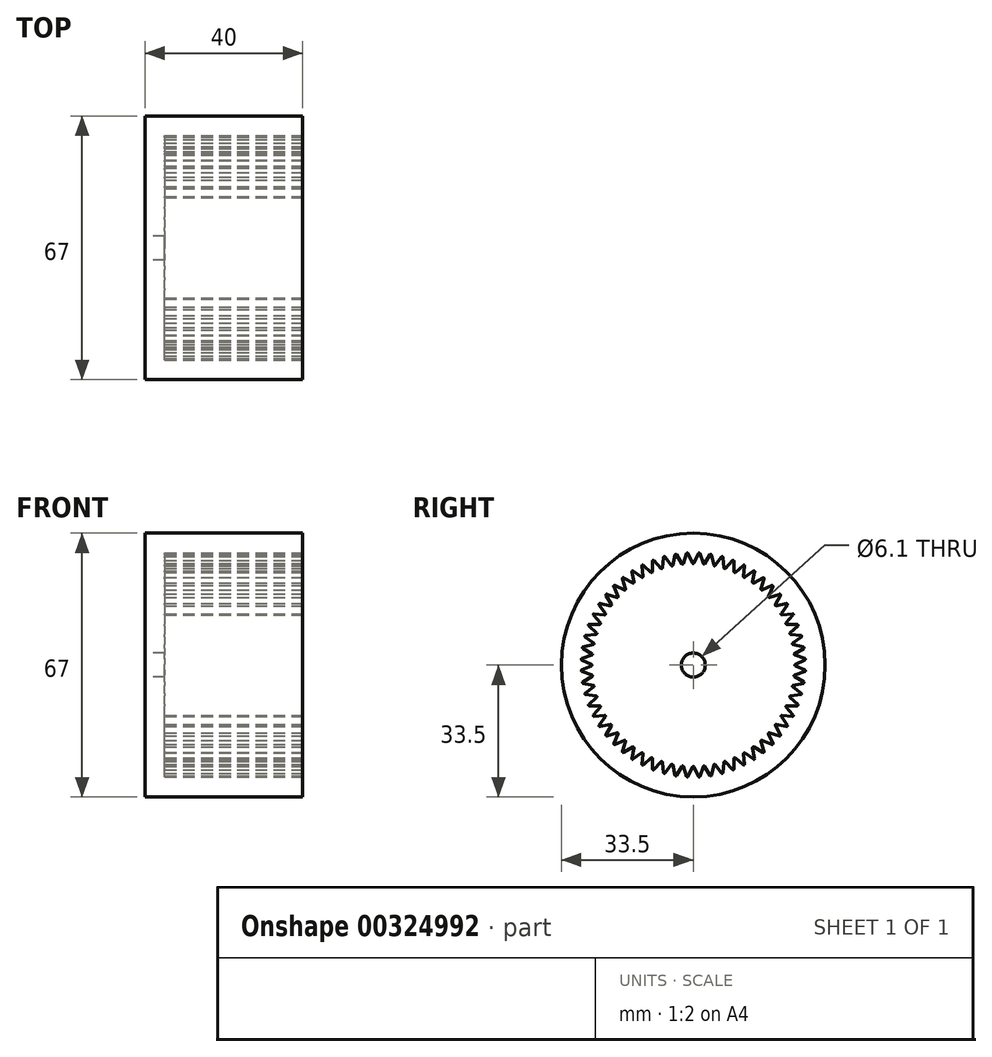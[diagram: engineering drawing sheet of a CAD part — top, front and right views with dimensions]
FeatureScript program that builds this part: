
annotation { "Feature Type Name" : "Feature", "Feature Type Description" : "" }
export const myFeature = defineFeature(function(context is Context, id is Id, definition is map)
    precondition{}
    {
        {
            var Q0;
            Q0=qCreatedBy(makeId("Right.planeOp"),FACE);
            var sketch = newSketch(context, id + "F0", { "sketchPlane" : qUnion([Q0])});
            skCircle(sketch, "E0", {"center": v(0, 0) * mm, "radius": 33.5 * mm});
            skSolve(sketch);
        }
        {
            var Q0;
            Q0 = qSketchRegion(id + "F0", true);
            extrude(context, id + "F1", {"entities" : qUnion([Q0]), "depth" : 40 * mm});
        }
        {
            var Q0;
            Q0=makeQuery(id+"F1.opExtrude","CAP_FACE",FACE,{"disambiguationData":[OSD([sQuery(id+"F0.wireOp",EDGE,"E0")])],"isStart":false});
            var sketch = newSketch(context, id + "F2", { "sketchPlane" : qUnion([Q0])});
            skLineSegment(sketch, "E1", {"start": v(-1.3, 28.34) * mm, "end": v(-0.18, 25.9) * mm});
            skLineSegment(sketch, "E2.MirrorCS", {"start": v(1.3, 28.34) * mm, "end": v(0.18, 25.9) * mm});
            skCircle(sketch, "E3", {"center": v(0, 0) * mm, "radius": 28.5 * mm, "construction": true});
            skPoint(sketch, "E4.visualSharp", {"position": v(0, 25.5) * mm});
            skArc(sketch, "E4.filletArc", {"start": v(-0.18, 25.9) * mm, "mid": v(0, 25.78) * mm, "end": v(0.18, 25.9) * mm});
            skArc(sketch, "E5", {"start": v(-1.3, 28.34) * mm, "mid": v(-1.5, 28.46) * mm, "end": v(-1.67, 28.32) * mm});
            skPoint(sketch, "E6.1.0", {"position": v(-2.67, 25.36) * mm});
            skLineSegment(sketch, "E6.1.1", {"start": v(-1.67, 28.32) * mm, "end": v(-2.53, 25.78) * mm});
            skLineSegment(sketch, "E6.1.2", {"start": v(-4.25, 28.05) * mm, "end": v(-2.89, 25.74) * mm});
            skArc(sketch, "E6.1.3", {"start": v(-2.89, 25.74) * mm, "mid": v(-2.7, 25.64) * mm, "end": v(-2.53, 25.78) * mm});
            skArc(sketch, "E6.1.4", {"start": v(-4.25, 28.05) * mm, "mid": v(-4.46, 28.15) * mm, "end": v(-4.62, 28) * mm});
            skPoint(sketch, "E6.2.0", {"position": v(-5.3, 24.94) * mm});
            skLineSegment(sketch, "E6.2.1", {"start": v(-4.62, 28) * mm, "end": v(-5.2, 25.37) * mm});
            skLineSegment(sketch, "E6.2.2", {"start": v(-7.16, 27.45) * mm, "end": v(-5.56, 25.3) * mm});
            skArc(sketch, "E6.2.3", {"start": v(-5.56, 25.3) * mm, "mid": v(-5.36, 25.22) * mm, "end": v(-5.2, 25.37) * mm});
            skArc(sketch, "E6.2.4", {"start": v(-7.16, 27.45) * mm, "mid": v(-7.38, 27.53) * mm, "end": v(-7.52, 27.36) * mm});
            skPoint(sketch, "E6.3.0", {"position": v(-7.88, 24.25) * mm});
            skLineSegment(sketch, "E6.3.1", {"start": v(-7.52, 27.36) * mm, "end": v(-7.83, 24.69) * mm});
            skLineSegment(sketch, "E6.3.2", {"start": v(-10, 26.56) * mm, "end": v(-8.18, 24.57) * mm});
            skArc(sketch, "E6.3.3", {"start": v(-8.18, 24.57) * mm, "mid": v(-7.97, 24.52) * mm, "end": v(-7.83, 24.69) * mm});
            skArc(sketch, "E6.3.4", {"start": v(-10, 26.56) * mm, "mid": v(-10.21, 26.6) * mm, "end": v(-10.34, 26.42) * mm});
            skPoint(sketch, "E6.4.0", {"position": v(-10.37, 23.3) * mm});
            skLineSegment(sketch, "E6.4.1", {"start": v(-10.34, 26.42) * mm, "end": v(-10.37, 23.73) * mm});
            skLineSegment(sketch, "E6.4.2", {"start": v(-12.72, 25.37) * mm, "end": v(-10.7, 23.59) * mm});
            skArc(sketch, "E6.4.3", {"start": v(-10.7, 23.59) * mm, "mid": v(-10.49, 23.55) * mm, "end": v(-10.37, 23.73) * mm});
            skArc(sketch, "E6.4.4", {"start": v(-12.72, 25.37) * mm, "mid": v(-12.94, 25.4) * mm, "end": v(-13.05, 25.2) * mm});
            skPoint(sketch, "E6.5.0", {"position": v(-12.75, 22.08) * mm});
            skLineSegment(sketch, "E6.5.1", {"start": v(-13.05, 25.2) * mm, "end": v(-12.8, 22.52) * mm});
            skLineSegment(sketch, "E6.5.2", {"start": v(-15.3, 23.9) * mm, "end": v(-13.1, 22.34) * mm});
            skArc(sketch, "E6.5.3", {"start": v(-13.1, 22.34) * mm, "mid": v(-12.9, 22.33) * mm, "end": v(-12.8, 22.52) * mm});
            skArc(sketch, "E6.5.4", {"start": v(-15.3, 23.9) * mm, "mid": v(-15.52, 23.9) * mm, "end": v(-15.6, 23.7) * mm});
            skPoint(sketch, "E6.6.0", {"position": v(-14.99, 20.63) * mm});
            skLineSegment(sketch, "E6.6.1", {"start": v(-15.6, 23.7) * mm, "end": v(-15.08, 21.06) * mm});
            skLineSegment(sketch, "E6.6.2", {"start": v(-17.71, 22.17) * mm, "end": v(-15.37, 20.85) * mm});
            skArc(sketch, "E6.6.3", {"start": v(-15.37, 20.85) * mm, "mid": v(-15.15, 20.86) * mm, "end": v(-15.08, 21.06) * mm});
            skArc(sketch, "E6.6.4", {"start": v(-17.71, 22.17) * mm, "mid": v(-17.94, 22.15) * mm, "end": v(-18, 21.93) * mm});
            skPoint(sketch, "E6.7.0", {"position": v(-17.06, 18.95) * mm});
            skLineSegment(sketch, "E6.7.1", {"start": v(-18, 21.93) * mm, "end": v(-17.2, 19.37) * mm});
            skLineSegment(sketch, "E6.7.2", {"start": v(-19.93, 20.2) * mm, "end": v(-17.46, 19.12) * mm});
            skArc(sketch, "E6.7.3", {"start": v(-17.46, 19.12) * mm, "mid": v(-17.25, 19.16) * mm, "end": v(-17.2, 19.37) * mm});
            skArc(sketch, "E6.7.4", {"start": v(-19.93, 20.2) * mm, "mid": v(-20.15, 20.15) * mm, "end": v(-20.2, 19.93) * mm});
            skPoint(sketch, "E6.8.0", {"position": v(-18.95, 17.06) * mm});
            skLineSegment(sketch, "E6.8.1", {"start": v(-20.2, 19.93) * mm, "end": v(-19.12, 17.46) * mm});
            skLineSegment(sketch, "E6.8.2", {"start": v(-21.93, 18) * mm, "end": v(-19.37, 17.2) * mm});
            skArc(sketch, "E6.8.3", {"start": v(-19.37, 17.2) * mm, "mid": v(-19.16, 17.25) * mm, "end": v(-19.12, 17.46) * mm});
            skArc(sketch, "E6.8.4", {"start": v(-21.93, 18) * mm, "mid": v(-22.15, 17.94) * mm, "end": v(-22.17, 17.71) * mm});
            skPoint(sketch, "E6.9.0", {"position": v(-20.63, 14.99) * mm});
            skLineSegment(sketch, "E6.9.1", {"start": v(-22.17, 17.71) * mm, "end": v(-20.85, 15.37) * mm});
            skLineSegment(sketch, "E6.9.2", {"start": v(-23.7, 15.6) * mm, "end": v(-21.06, 15.08) * mm});
            skArc(sketch, "E6.9.3", {"start": v(-21.06, 15.08) * mm, "mid": v(-20.86, 15.15) * mm, "end": v(-20.85, 15.37) * mm});
            skArc(sketch, "E6.9.4", {"start": v(-23.7, 15.6) * mm, "mid": v(-23.9, 15.52) * mm, "end": v(-23.9, 15.3) * mm});
            skPoint(sketch, "E6.10.0", {"position": v(-22.08, 12.75) * mm});
            skLineSegment(sketch, "E6.10.1", {"start": v(-23.9, 15.3) * mm, "end": v(-22.34, 13.1) * mm});
            skLineSegment(sketch, "E6.10.2", {"start": v(-25.2, 13.05) * mm, "end": v(-22.52, 12.8) * mm});
            skArc(sketch, "E6.10.3", {"start": v(-22.52, 12.8) * mm, "mid": v(-22.33, 12.9) * mm, "end": v(-22.34, 13.1) * mm});
            skArc(sketch, "E6.10.4", {"start": v(-25.2, 13.05) * mm, "mid": v(-25.4, 12.94) * mm, "end": v(-25.37, 12.72) * mm});
            skPoint(sketch, "E6.11.0", {"position": v(-23.3, 10.37) * mm});
            skLineSegment(sketch, "E6.11.1", {"start": v(-25.37, 12.72) * mm, "end": v(-23.59, 10.7) * mm});
            skLineSegment(sketch, "E6.11.2", {"start": v(-26.42, 10.34) * mm, "end": v(-23.73, 10.37) * mm});
            skArc(sketch, "E6.11.3", {"start": v(-23.73, 10.37) * mm, "mid": v(-23.55, 10.49) * mm, "end": v(-23.59, 10.7) * mm});
            skArc(sketch, "E6.11.4", {"start": v(-26.42, 10.34) * mm, "mid": v(-26.6, 10.21) * mm, "end": v(-26.56, 10) * mm});
            skPoint(sketch, "E6.12.0", {"position": v(-24.25, 7.88) * mm});
            skLineSegment(sketch, "E6.12.1", {"start": v(-26.56, 10) * mm, "end": v(-24.57, 8.18) * mm});
            skLineSegment(sketch, "E6.12.2", {"start": v(-27.36, 7.52) * mm, "end": v(-24.69, 7.83) * mm});
            skArc(sketch, "E6.12.3", {"start": v(-24.69, 7.83) * mm, "mid": v(-24.52, 7.97) * mm, "end": v(-24.57, 8.18) * mm});
            skArc(sketch, "E6.12.4", {"start": v(-27.36, 7.52) * mm, "mid": v(-27.53, 7.38) * mm, "end": v(-27.45, 7.16) * mm});
            skPoint(sketch, "E6.13.0", {"position": v(-24.94, 5.3) * mm});
            skLineSegment(sketch, "E6.13.1", {"start": v(-27.45, 7.16) * mm, "end": v(-25.3, 5.56) * mm});
            skLineSegment(sketch, "E6.13.2", {"start": v(-28, 4.62) * mm, "end": v(-25.37, 5.2) * mm});
            skArc(sketch, "E6.13.3", {"start": v(-25.37, 5.2) * mm, "mid": v(-25.22, 5.36) * mm, "end": v(-25.3, 5.56) * mm});
            skArc(sketch, "E6.13.4", {"start": v(-28, 4.62) * mm, "mid": v(-28.15, 4.46) * mm, "end": v(-28.05, 4.25) * mm});
            skPoint(sketch, "E6.14.0", {"position": v(-25.36, 2.67) * mm});
            skLineSegment(sketch, "E6.14.1", {"start": v(-28.05, 4.25) * mm, "end": v(-25.74, 2.89) * mm});
            skLineSegment(sketch, "E6.14.2", {"start": v(-28.32, 1.67) * mm, "end": v(-25.78, 2.53) * mm});
            skArc(sketch, "E6.14.3", {"start": v(-25.78, 2.53) * mm, "mid": v(-25.64, 2.7) * mm, "end": v(-25.74, 2.89) * mm});
            skArc(sketch, "E6.14.4", {"start": v(-28.32, 1.67) * mm, "mid": v(-28.46, 1.5) * mm, "end": v(-28.34, 1.3) * mm});
            skPoint(sketch, "E6.15.0", {"position": v(-25.5, 0) * mm});
            skLineSegment(sketch, "E6.15.1", {"start": v(-28.34, 1.3) * mm, "end": v(-25.9, 0.18) * mm});
            skLineSegment(sketch, "E6.15.2", {"start": v(-28.34, -1.3) * mm, "end": v(-25.9, -0.18) * mm});
            skArc(sketch, "E6.15.3", {"start": v(-25.9, -0.18) * mm, "mid": v(-25.78, 0) * mm, "end": v(-25.9, 0.18) * mm});
            skArc(sketch, "E6.15.4", {"start": v(-28.34, -1.3) * mm, "mid": v(-28.46, -1.5) * mm, "end": v(-28.32, -1.67) * mm});
            skPoint(sketch, "E6.16.0", {"position": v(-25.36, -2.67) * mm});
            skLineSegment(sketch, "E6.16.1", {"start": v(-28.32, -1.67) * mm, "end": v(-25.78, -2.53) * mm});
            skLineSegment(sketch, "E6.16.2", {"start": v(-28.05, -4.25) * mm, "end": v(-25.74, -2.89) * mm});
            skArc(sketch, "E6.16.3", {"start": v(-25.74, -2.89) * mm, "mid": v(-25.64, -2.7) * mm, "end": v(-25.78, -2.53) * mm});
            skArc(sketch, "E6.16.4", {"start": v(-28.05, -4.25) * mm, "mid": v(-28.15, -4.46) * mm, "end": v(-28, -4.62) * mm});
            skPoint(sketch, "E6.17.0", {"position": v(-24.94, -5.3) * mm});
            skLineSegment(sketch, "E6.17.1", {"start": v(-28, -4.62) * mm, "end": v(-25.37, -5.2) * mm});
            skLineSegment(sketch, "E6.17.2", {"start": v(-27.45, -7.16) * mm, "end": v(-25.3, -5.56) * mm});
            skArc(sketch, "E6.17.3", {"start": v(-25.3, -5.56) * mm, "mid": v(-25.22, -5.36) * mm, "end": v(-25.37, -5.2) * mm});
            skArc(sketch, "E6.17.4", {"start": v(-27.45, -7.16) * mm, "mid": v(-27.53, -7.38) * mm, "end": v(-27.36, -7.52) * mm});
            skPoint(sketch, "E6.18.0", {"position": v(-24.25, -7.88) * mm});
            skLineSegment(sketch, "E6.18.1", {"start": v(-27.36, -7.52) * mm, "end": v(-24.69, -7.83) * mm});
            skLineSegment(sketch, "E6.18.2", {"start": v(-26.56, -10) * mm, "end": v(-24.57, -8.18) * mm});
            skArc(sketch, "E6.18.3", {"start": v(-24.57, -8.18) * mm, "mid": v(-24.52, -7.97) * mm, "end": v(-24.69, -7.83) * mm});
            skArc(sketch, "E6.18.4", {"start": v(-26.56, -10) * mm, "mid": v(-26.6, -10.21) * mm, "end": v(-26.42, -10.34) * mm});
            skPoint(sketch, "E6.19.0", {"position": v(-23.3, -10.37) * mm});
            skLineSegment(sketch, "E6.19.1", {"start": v(-26.42, -10.34) * mm, "end": v(-23.73, -10.37) * mm});
            skLineSegment(sketch, "E6.19.2", {"start": v(-25.37, -12.72) * mm, "end": v(-23.59, -10.7) * mm});
            skArc(sketch, "E6.19.3", {"start": v(-23.59, -10.7) * mm, "mid": v(-23.55, -10.49) * mm, "end": v(-23.73, -10.37) * mm});
            skArc(sketch, "E6.19.4", {"start": v(-25.37, -12.72) * mm, "mid": v(-25.4, -12.94) * mm, "end": v(-25.2, -13.05) * mm});
            skPoint(sketch, "E6.20.0", {"position": v(-22.08, -12.75) * mm});
            skLineSegment(sketch, "E6.20.1", {"start": v(-25.2, -13.05) * mm, "end": v(-22.52, -12.8) * mm});
            skLineSegment(sketch, "E6.20.2", {"start": v(-23.9, -15.3) * mm, "end": v(-22.34, -13.1) * mm});
            skArc(sketch, "E6.20.3", {"start": v(-22.34, -13.1) * mm, "mid": v(-22.33, -12.9) * mm, "end": v(-22.52, -12.8) * mm});
            skArc(sketch, "E6.20.4", {"start": v(-23.9, -15.3) * mm, "mid": v(-23.9, -15.52) * mm, "end": v(-23.7, -15.6) * mm});
            skPoint(sketch, "E6.21.0", {"position": v(-20.63, -14.99) * mm});
            skLineSegment(sketch, "E6.21.1", {"start": v(-23.7, -15.6) * mm, "end": v(-21.06, -15.08) * mm});
            skLineSegment(sketch, "E6.21.2", {"start": v(-22.17, -17.71) * mm, "end": v(-20.85, -15.37) * mm});
            skArc(sketch, "E6.21.3", {"start": v(-20.85, -15.37) * mm, "mid": v(-20.86, -15.15) * mm, "end": v(-21.06, -15.08) * mm});
            skArc(sketch, "E6.21.4", {"start": v(-22.17, -17.71) * mm, "mid": v(-22.15, -17.94) * mm, "end": v(-21.93, -18) * mm});
            skPoint(sketch, "E6.22.0", {"position": v(-18.95, -17.06) * mm});
            skLineSegment(sketch, "E6.22.1", {"start": v(-21.93, -18) * mm, "end": v(-19.37, -17.2) * mm});
            skLineSegment(sketch, "E6.22.2", {"start": v(-20.2, -19.93) * mm, "end": v(-19.12, -17.46) * mm});
            skArc(sketch, "E6.22.3", {"start": v(-19.12, -17.46) * mm, "mid": v(-19.16, -17.25) * mm, "end": v(-19.37, -17.2) * mm});
            skArc(sketch, "E6.22.4", {"start": v(-20.2, -19.93) * mm, "mid": v(-20.15, -20.15) * mm, "end": v(-19.93, -20.2) * mm});
            skPoint(sketch, "E6.23.0", {"position": v(-17.06, -18.95) * mm});
            skLineSegment(sketch, "E6.23.1", {"start": v(-19.93, -20.2) * mm, "end": v(-17.46, -19.12) * mm});
            skLineSegment(sketch, "E6.23.2", {"start": v(-18, -21.93) * mm, "end": v(-17.2, -19.37) * mm});
            skArc(sketch, "E6.23.3", {"start": v(-17.2, -19.37) * mm, "mid": v(-17.25, -19.16) * mm, "end": v(-17.46, -19.12) * mm});
            skArc(sketch, "E6.23.4", {"start": v(-18, -21.93) * mm, "mid": v(-17.94, -22.15) * mm, "end": v(-17.71, -22.17) * mm});
            skPoint(sketch, "E6.24.0", {"position": v(-14.99, -20.63) * mm});
            skLineSegment(sketch, "E6.24.1", {"start": v(-17.71, -22.17) * mm, "end": v(-15.37, -20.85) * mm});
            skLineSegment(sketch, "E6.24.2", {"start": v(-15.6, -23.7) * mm, "end": v(-15.08, -21.06) * mm});
            skArc(sketch, "E6.24.3", {"start": v(-15.08, -21.06) * mm, "mid": v(-15.15, -20.86) * mm, "end": v(-15.37, -20.85) * mm});
            skArc(sketch, "E6.24.4", {"start": v(-15.6, -23.7) * mm, "mid": v(-15.52, -23.9) * mm, "end": v(-15.3, -23.9) * mm});
            skPoint(sketch, "E6.25.0", {"position": v(-12.75, -22.08) * mm});
            skLineSegment(sketch, "E6.25.1", {"start": v(-15.3, -23.9) * mm, "end": v(-13.1, -22.34) * mm});
            skLineSegment(sketch, "E6.25.2", {"start": v(-13.05, -25.2) * mm, "end": v(-12.8, -22.52) * mm});
            skArc(sketch, "E6.25.3", {"start": v(-12.8, -22.52) * mm, "mid": v(-12.9, -22.33) * mm, "end": v(-13.1, -22.34) * mm});
            skArc(sketch, "E6.25.4", {"start": v(-13.05, -25.2) * mm, "mid": v(-12.94, -25.4) * mm, "end": v(-12.72, -25.37) * mm});
            skPoint(sketch, "E6.26.0", {"position": v(-10.37, -23.3) * mm});
            skLineSegment(sketch, "E6.26.1", {"start": v(-12.72, -25.37) * mm, "end": v(-10.7, -23.59) * mm});
            skLineSegment(sketch, "E6.26.2", {"start": v(-10.34, -26.42) * mm, "end": v(-10.37, -23.73) * mm});
            skArc(sketch, "E6.26.3", {"start": v(-10.37, -23.73) * mm, "mid": v(-10.49, -23.55) * mm, "end": v(-10.7, -23.59) * mm});
            skArc(sketch, "E6.26.4", {"start": v(-10.34, -26.42) * mm, "mid": v(-10.21, -26.6) * mm, "end": v(-10, -26.56) * mm});
            skPoint(sketch, "E6.27.0", {"position": v(-7.88, -24.25) * mm});
            skLineSegment(sketch, "E6.27.1", {"start": v(-10, -26.56) * mm, "end": v(-8.18, -24.57) * mm});
            skLineSegment(sketch, "E6.27.2", {"start": v(-7.52, -27.36) * mm, "end": v(-7.83, -24.69) * mm});
            skArc(sketch, "E6.27.3", {"start": v(-7.83, -24.69) * mm, "mid": v(-7.97, -24.52) * mm, "end": v(-8.18, -24.57) * mm});
            skArc(sketch, "E6.27.4", {"start": v(-7.52, -27.36) * mm, "mid": v(-7.38, -27.53) * mm, "end": v(-7.16, -27.45) * mm});
            skPoint(sketch, "E6.28.0", {"position": v(-5.3, -24.94) * mm});
            skLineSegment(sketch, "E6.28.1", {"start": v(-7.16, -27.45) * mm, "end": v(-5.56, -25.3) * mm});
            skLineSegment(sketch, "E6.28.2", {"start": v(-4.62, -28) * mm, "end": v(-5.2, -25.37) * mm});
            skArc(sketch, "E6.28.3", {"start": v(-5.2, -25.37) * mm, "mid": v(-5.36, -25.22) * mm, "end": v(-5.56, -25.3) * mm});
            skArc(sketch, "E6.28.4", {"start": v(-4.62, -28) * mm, "mid": v(-4.46, -28.15) * mm, "end": v(-4.25, -28.05) * mm});
            skPoint(sketch, "E6.29.0", {"position": v(-2.67, -25.36) * mm});
            skLineSegment(sketch, "E6.29.1", {"start": v(-4.25, -28.05) * mm, "end": v(-2.89, -25.74) * mm});
            skLineSegment(sketch, "E6.29.2", {"start": v(-1.67, -28.32) * mm, "end": v(-2.53, -25.78) * mm});
            skArc(sketch, "E6.29.3", {"start": v(-2.53, -25.78) * mm, "mid": v(-2.7, -25.64) * mm, "end": v(-2.89, -25.74) * mm});
            skArc(sketch, "E6.29.4", {"start": v(-1.67, -28.32) * mm, "mid": v(-1.5, -28.46) * mm, "end": v(-1.3, -28.34) * mm});
            skPoint(sketch, "E6.30.0", {"position": v(0, -25.5) * mm});
            skLineSegment(sketch, "E6.30.1", {"start": v(-1.3, -28.34) * mm, "end": v(-0.18, -25.9) * mm});
            skLineSegment(sketch, "E6.30.2", {"start": v(1.3, -28.34) * mm, "end": v(0.18, -25.9) * mm});
            skArc(sketch, "E6.30.3", {"start": v(0.18, -25.9) * mm, "mid": v(0, -25.78) * mm, "end": v(-0.18, -25.9) * mm});
            skArc(sketch, "E6.30.4", {"start": v(1.3, -28.34) * mm, "mid": v(1.5, -28.46) * mm, "end": v(1.67, -28.32) * mm});
            skPoint(sketch, "E6.31.0", {"position": v(2.67, -25.36) * mm});
            skLineSegment(sketch, "E6.31.1", {"start": v(1.67, -28.32) * mm, "end": v(2.53, -25.78) * mm});
            skLineSegment(sketch, "E6.31.2", {"start": v(4.25, -28.05) * mm, "end": v(2.89, -25.74) * mm});
            skArc(sketch, "E6.31.3", {"start": v(2.89, -25.74) * mm, "mid": v(2.7, -25.64) * mm, "end": v(2.53, -25.78) * mm});
            skArc(sketch, "E6.31.4", {"start": v(4.25, -28.05) * mm, "mid": v(4.46, -28.15) * mm, "end": v(4.62, -28) * mm});
            skPoint(sketch, "E6.32.0", {"position": v(5.3, -24.94) * mm});
            skLineSegment(sketch, "E6.32.1", {"start": v(4.62, -28) * mm, "end": v(5.2, -25.37) * mm});
            skLineSegment(sketch, "E6.32.2", {"start": v(7.16, -27.45) * mm, "end": v(5.56, -25.3) * mm});
            skArc(sketch, "E6.32.3", {"start": v(5.56, -25.3) * mm, "mid": v(5.36, -25.22) * mm, "end": v(5.2, -25.37) * mm});
            skArc(sketch, "E6.32.4", {"start": v(7.16, -27.45) * mm, "mid": v(7.38, -27.53) * mm, "end": v(7.52, -27.36) * mm});
            skPoint(sketch, "E6.33.0", {"position": v(7.88, -24.25) * mm});
            skLineSegment(sketch, "E6.33.1", {"start": v(7.52, -27.36) * mm, "end": v(7.83, -24.69) * mm});
            skLineSegment(sketch, "E6.33.2", {"start": v(10, -26.56) * mm, "end": v(8.18, -24.57) * mm});
            skArc(sketch, "E6.33.3", {"start": v(8.18, -24.57) * mm, "mid": v(7.97, -24.52) * mm, "end": v(7.83, -24.69) * mm});
            skArc(sketch, "E6.33.4", {"start": v(10, -26.56) * mm, "mid": v(10.21, -26.6) * mm, "end": v(10.34, -26.42) * mm});
            skPoint(sketch, "E6.34.0", {"position": v(10.37, -23.3) * mm});
            skLineSegment(sketch, "E6.34.1", {"start": v(10.34, -26.42) * mm, "end": v(10.37, -23.73) * mm});
            skLineSegment(sketch, "E6.34.2", {"start": v(12.72, -25.37) * mm, "end": v(10.7, -23.59) * mm});
            skArc(sketch, "E6.34.3", {"start": v(10.7, -23.59) * mm, "mid": v(10.49, -23.55) * mm, "end": v(10.37, -23.73) * mm});
            skArc(sketch, "E6.34.4", {"start": v(12.72, -25.37) * mm, "mid": v(12.94, -25.4) * mm, "end": v(13.05, -25.2) * mm});
            skPoint(sketch, "E6.35.0", {"position": v(12.75, -22.08) * mm});
            skLineSegment(sketch, "E6.35.1", {"start": v(13.05, -25.2) * mm, "end": v(12.8, -22.52) * mm});
            skLineSegment(sketch, "E6.35.2", {"start": v(15.3, -23.9) * mm, "end": v(13.1, -22.34) * mm});
            skArc(sketch, "E6.35.3", {"start": v(13.1, -22.34) * mm, "mid": v(12.9, -22.33) * mm, "end": v(12.8, -22.52) * mm});
            skArc(sketch, "E6.35.4", {"start": v(15.3, -23.9) * mm, "mid": v(15.52, -23.9) * mm, "end": v(15.6, -23.7) * mm});
            skPoint(sketch, "E6.36.0", {"position": v(14.99, -20.63) * mm});
            skLineSegment(sketch, "E6.36.1", {"start": v(15.6, -23.7) * mm, "end": v(15.08, -21.06) * mm});
            skLineSegment(sketch, "E6.36.2", {"start": v(17.71, -22.17) * mm, "end": v(15.37, -20.85) * mm});
            skArc(sketch, "E6.36.3", {"start": v(15.37, -20.85) * mm, "mid": v(15.15, -20.86) * mm, "end": v(15.08, -21.06) * mm});
            skArc(sketch, "E6.36.4", {"start": v(17.71, -22.17) * mm, "mid": v(17.94, -22.15) * mm, "end": v(18, -21.93) * mm});
            skPoint(sketch, "E6.37.0", {"position": v(17.06, -18.95) * mm});
            skLineSegment(sketch, "E6.37.1", {"start": v(18, -21.93) * mm, "end": v(17.2, -19.37) * mm});
            skLineSegment(sketch, "E6.37.2", {"start": v(19.93, -20.2) * mm, "end": v(17.46, -19.12) * mm});
            skArc(sketch, "E6.37.3", {"start": v(17.46, -19.12) * mm, "mid": v(17.25, -19.16) * mm, "end": v(17.2, -19.37) * mm});
            skArc(sketch, "E6.37.4", {"start": v(19.93, -20.2) * mm, "mid": v(20.15, -20.15) * mm, "end": v(20.2, -19.93) * mm});
            skPoint(sketch, "E6.38.0", {"position": v(18.95, -17.06) * mm});
            skLineSegment(sketch, "E6.38.1", {"start": v(20.2, -19.93) * mm, "end": v(19.12, -17.46) * mm});
            skLineSegment(sketch, "E6.38.2", {"start": v(21.93, -18) * mm, "end": v(19.37, -17.2) * mm});
            skArc(sketch, "E6.38.3", {"start": v(19.37, -17.2) * mm, "mid": v(19.16, -17.25) * mm, "end": v(19.12, -17.46) * mm});
            skArc(sketch, "E6.38.4", {"start": v(21.93, -18) * mm, "mid": v(22.15, -17.94) * mm, "end": v(22.17, -17.71) * mm});
            skPoint(sketch, "E6.39.0", {"position": v(20.63, -14.99) * mm});
            skLineSegment(sketch, "E6.39.1", {"start": v(22.17, -17.71) * mm, "end": v(20.85, -15.37) * mm});
            skLineSegment(sketch, "E6.39.2", {"start": v(23.7, -15.6) * mm, "end": v(21.06, -15.08) * mm});
            skArc(sketch, "E6.39.3", {"start": v(21.06, -15.08) * mm, "mid": v(20.86, -15.15) * mm, "end": v(20.85, -15.37) * mm});
            skArc(sketch, "E6.39.4", {"start": v(23.7, -15.6) * mm, "mid": v(23.9, -15.52) * mm, "end": v(23.9, -15.3) * mm});
            skPoint(sketch, "E6.40.0", {"position": v(22.08, -12.75) * mm});
            skLineSegment(sketch, "E6.40.1", {"start": v(23.9, -15.3) * mm, "end": v(22.34, -13.1) * mm});
            skLineSegment(sketch, "E6.40.2", {"start": v(25.2, -13.05) * mm, "end": v(22.52, -12.8) * mm});
            skArc(sketch, "E6.40.3", {"start": v(22.52, -12.8) * mm, "mid": v(22.33, -12.9) * mm, "end": v(22.34, -13.1) * mm});
            skArc(sketch, "E6.40.4", {"start": v(25.2, -13.05) * mm, "mid": v(25.4, -12.94) * mm, "end": v(25.37, -12.72) * mm});
            skPoint(sketch, "E6.41.0", {"position": v(23.3, -10.37) * mm});
            skLineSegment(sketch, "E6.41.1", {"start": v(25.37, -12.72) * mm, "end": v(23.59, -10.7) * mm});
            skLineSegment(sketch, "E6.41.2", {"start": v(26.42, -10.34) * mm, "end": v(23.73, -10.37) * mm});
            skArc(sketch, "E6.41.3", {"start": v(23.73, -10.37) * mm, "mid": v(23.55, -10.49) * mm, "end": v(23.59, -10.7) * mm});
            skArc(sketch, "E6.41.4", {"start": v(26.42, -10.34) * mm, "mid": v(26.6, -10.21) * mm, "end": v(26.56, -10) * mm});
            skPoint(sketch, "E6.42.0", {"position": v(24.25, -7.88) * mm});
            skLineSegment(sketch, "E6.42.1", {"start": v(26.56, -10) * mm, "end": v(24.57, -8.18) * mm});
            skLineSegment(sketch, "E6.42.2", {"start": v(27.36, -7.52) * mm, "end": v(24.69, -7.83) * mm});
            skArc(sketch, "E6.42.3", {"start": v(24.69, -7.83) * mm, "mid": v(24.52, -7.97) * mm, "end": v(24.57, -8.18) * mm});
            skArc(sketch, "E6.42.4", {"start": v(27.36, -7.52) * mm, "mid": v(27.53, -7.38) * mm, "end": v(27.45, -7.16) * mm});
            skPoint(sketch, "E6.43.0", {"position": v(24.94, -5.3) * mm});
            skLineSegment(sketch, "E6.43.1", {"start": v(27.45, -7.16) * mm, "end": v(25.3, -5.56) * mm});
            skLineSegment(sketch, "E6.43.2", {"start": v(28, -4.62) * mm, "end": v(25.37, -5.2) * mm});
            skArc(sketch, "E6.43.3", {"start": v(25.37, -5.2) * mm, "mid": v(25.22, -5.36) * mm, "end": v(25.3, -5.56) * mm});
            skArc(sketch, "E6.43.4", {"start": v(28, -4.62) * mm, "mid": v(28.15, -4.46) * mm, "end": v(28.05, -4.25) * mm});
            skPoint(sketch, "E6.44.0", {"position": v(25.36, -2.67) * mm});
            skLineSegment(sketch, "E6.44.1", {"start": v(28.05, -4.25) * mm, "end": v(25.74, -2.89) * mm});
            skLineSegment(sketch, "E6.44.2", {"start": v(28.32, -1.67) * mm, "end": v(25.78, -2.53) * mm});
            skArc(sketch, "E6.44.3", {"start": v(25.78, -2.53) * mm, "mid": v(25.64, -2.7) * mm, "end": v(25.74, -2.89) * mm});
            skArc(sketch, "E6.44.4", {"start": v(28.32, -1.67) * mm, "mid": v(28.46, -1.5) * mm, "end": v(28.34, -1.3) * mm});
            skPoint(sketch, "E6.45.0", {"position": v(25.5, 0) * mm});
            skLineSegment(sketch, "E6.45.1", {"start": v(28.34, -1.3) * mm, "end": v(25.9, -0.18) * mm});
            skLineSegment(sketch, "E6.45.2", {"start": v(28.34, 1.3) * mm, "end": v(25.9, 0.18) * mm});
            skArc(sketch, "E6.45.3", {"start": v(25.9, 0.18) * mm, "mid": v(25.78, 0) * mm, "end": v(25.9, -0.18) * mm});
            skArc(sketch, "E6.45.4", {"start": v(28.34, 1.3) * mm, "mid": v(28.46, 1.5) * mm, "end": v(28.32, 1.67) * mm});
            skPoint(sketch, "E6.46.0", {"position": v(25.36, 2.67) * mm});
            skLineSegment(sketch, "E6.46.1", {"start": v(28.32, 1.67) * mm, "end": v(25.78, 2.53) * mm});
            skLineSegment(sketch, "E6.46.2", {"start": v(28.05, 4.25) * mm, "end": v(25.74, 2.89) * mm});
            skArc(sketch, "E6.46.3", {"start": v(25.74, 2.89) * mm, "mid": v(25.64, 2.7) * mm, "end": v(25.78, 2.53) * mm});
            skArc(sketch, "E6.46.4", {"start": v(28.05, 4.25) * mm, "mid": v(28.15, 4.46) * mm, "end": v(28, 4.62) * mm});
            skPoint(sketch, "E6.47.0", {"position": v(24.94, 5.3) * mm});
            skLineSegment(sketch, "E6.47.1", {"start": v(28, 4.62) * mm, "end": v(25.37, 5.2) * mm});
            skLineSegment(sketch, "E6.47.2", {"start": v(27.45, 7.16) * mm, "end": v(25.3, 5.56) * mm});
            skArc(sketch, "E6.47.3", {"start": v(25.3, 5.56) * mm, "mid": v(25.22, 5.36) * mm, "end": v(25.37, 5.2) * mm});
            skArc(sketch, "E6.47.4", {"start": v(27.45, 7.16) * mm, "mid": v(27.53, 7.38) * mm, "end": v(27.36, 7.52) * mm});
            skPoint(sketch, "E6.48.0", {"position": v(24.25, 7.88) * mm});
            skLineSegment(sketch, "E6.48.1", {"start": v(27.36, 7.52) * mm, "end": v(24.69, 7.83) * mm});
            skLineSegment(sketch, "E6.48.2", {"start": v(26.56, 10) * mm, "end": v(24.57, 8.18) * mm});
            skArc(sketch, "E6.48.3", {"start": v(24.57, 8.18) * mm, "mid": v(24.52, 7.97) * mm, "end": v(24.69, 7.83) * mm});
            skArc(sketch, "E6.48.4", {"start": v(26.56, 10) * mm, "mid": v(26.6, 10.21) * mm, "end": v(26.42, 10.34) * mm});
            skPoint(sketch, "E6.49.0", {"position": v(23.3, 10.37) * mm});
            skLineSegment(sketch, "E6.49.1", {"start": v(26.42, 10.34) * mm, "end": v(23.73, 10.37) * mm});
            skLineSegment(sketch, "E6.49.2", {"start": v(25.37, 12.72) * mm, "end": v(23.59, 10.7) * mm});
            skArc(sketch, "E6.49.3", {"start": v(23.59, 10.7) * mm, "mid": v(23.55, 10.49) * mm, "end": v(23.73, 10.37) * mm});
            skArc(sketch, "E6.49.4", {"start": v(25.37, 12.72) * mm, "mid": v(25.4, 12.94) * mm, "end": v(25.2, 13.05) * mm});
            skPoint(sketch, "E6.50.0", {"position": v(22.08, 12.75) * mm});
            skLineSegment(sketch, "E6.50.1", {"start": v(25.2, 13.05) * mm, "end": v(22.52, 12.8) * mm});
            skLineSegment(sketch, "E6.50.2", {"start": v(23.9, 15.3) * mm, "end": v(22.34, 13.1) * mm});
            skArc(sketch, "E6.50.3", {"start": v(22.34, 13.1) * mm, "mid": v(22.33, 12.9) * mm, "end": v(22.52, 12.8) * mm});
            skArc(sketch, "E6.50.4", {"start": v(23.9, 15.3) * mm, "mid": v(23.9, 15.52) * mm, "end": v(23.7, 15.6) * mm});
            skPoint(sketch, "E6.51.0", {"position": v(20.63, 14.99) * mm});
            skLineSegment(sketch, "E6.51.1", {"start": v(23.7, 15.6) * mm, "end": v(21.06, 15.08) * mm});
            skLineSegment(sketch, "E6.51.2", {"start": v(22.17, 17.71) * mm, "end": v(20.85, 15.37) * mm});
            skArc(sketch, "E6.51.3", {"start": v(20.85, 15.37) * mm, "mid": v(20.86, 15.15) * mm, "end": v(21.06, 15.08) * mm});
            skArc(sketch, "E6.51.4", {"start": v(22.17, 17.71) * mm, "mid": v(22.15, 17.94) * mm, "end": v(21.93, 18) * mm});
            skPoint(sketch, "E6.52.0", {"position": v(18.95, 17.06) * mm});
            skLineSegment(sketch, "E6.52.1", {"start": v(21.93, 18) * mm, "end": v(19.37, 17.2) * mm});
            skLineSegment(sketch, "E6.52.2", {"start": v(20.2, 19.93) * mm, "end": v(19.12, 17.46) * mm});
            skArc(sketch, "E6.52.3", {"start": v(19.12, 17.46) * mm, "mid": v(19.16, 17.25) * mm, "end": v(19.37, 17.2) * mm});
            skArc(sketch, "E6.52.4", {"start": v(20.2, 19.93) * mm, "mid": v(20.15, 20.15) * mm, "end": v(19.93, 20.2) * mm});
            skPoint(sketch, "E6.53.0", {"position": v(17.06, 18.95) * mm});
            skLineSegment(sketch, "E6.53.1", {"start": v(19.93, 20.2) * mm, "end": v(17.46, 19.12) * mm});
            skLineSegment(sketch, "E6.53.2", {"start": v(18, 21.93) * mm, "end": v(17.2, 19.37) * mm});
            skArc(sketch, "E6.53.3", {"start": v(17.2, 19.37) * mm, "mid": v(17.25, 19.16) * mm, "end": v(17.46, 19.12) * mm});
            skArc(sketch, "E6.53.4", {"start": v(18, 21.93) * mm, "mid": v(17.94, 22.15) * mm, "end": v(17.71, 22.17) * mm});
            skPoint(sketch, "E6.54.0", {"position": v(14.99, 20.63) * mm});
            skLineSegment(sketch, "E6.54.1", {"start": v(17.71, 22.17) * mm, "end": v(15.37, 20.85) * mm});
            skLineSegment(sketch, "E6.54.2", {"start": v(15.6, 23.7) * mm, "end": v(15.08, 21.06) * mm});
            skArc(sketch, "E6.54.3", {"start": v(15.08, 21.06) * mm, "mid": v(15.15, 20.86) * mm, "end": v(15.37, 20.85) * mm});
            skArc(sketch, "E6.54.4", {"start": v(15.6, 23.7) * mm, "mid": v(15.52, 23.9) * mm, "end": v(15.3, 23.9) * mm});
            skPoint(sketch, "E6.55.0", {"position": v(12.75, 22.08) * mm});
            skLineSegment(sketch, "E6.55.1", {"start": v(15.3, 23.9) * mm, "end": v(13.1, 22.34) * mm});
            skLineSegment(sketch, "E6.55.2", {"start": v(13.05, 25.2) * mm, "end": v(12.8, 22.52) * mm});
            skArc(sketch, "E6.55.3", {"start": v(12.8, 22.52) * mm, "mid": v(12.9, 22.33) * mm, "end": v(13.1, 22.34) * mm});
            skArc(sketch, "E6.55.4", {"start": v(13.05, 25.2) * mm, "mid": v(12.94, 25.4) * mm, "end": v(12.72, 25.37) * mm});
            skPoint(sketch, "E6.56.0", {"position": v(10.37, 23.3) * mm});
            skLineSegment(sketch, "E6.56.1", {"start": v(12.72, 25.37) * mm, "end": v(10.7, 23.59) * mm});
            skLineSegment(sketch, "E6.56.2", {"start": v(10.34, 26.42) * mm, "end": v(10.37, 23.73) * mm});
            skArc(sketch, "E6.56.3", {"start": v(10.37, 23.73) * mm, "mid": v(10.49, 23.55) * mm, "end": v(10.7, 23.59) * mm});
            skArc(sketch, "E6.56.4", {"start": v(10.34, 26.42) * mm, "mid": v(10.21, 26.6) * mm, "end": v(10, 26.56) * mm});
            skPoint(sketch, "E6.57.0", {"position": v(7.88, 24.25) * mm});
            skLineSegment(sketch, "E6.57.1", {"start": v(10, 26.56) * mm, "end": v(8.18, 24.57) * mm});
            skLineSegment(sketch, "E6.57.2", {"start": v(7.52, 27.36) * mm, "end": v(7.83, 24.69) * mm});
            skArc(sketch, "E6.57.3", {"start": v(7.83, 24.69) * mm, "mid": v(7.97, 24.52) * mm, "end": v(8.18, 24.57) * mm});
            skArc(sketch, "E6.57.4", {"start": v(7.52, 27.36) * mm, "mid": v(7.38, 27.53) * mm, "end": v(7.16, 27.45) * mm});
            skPoint(sketch, "E6.58.0", {"position": v(5.3, 24.94) * mm});
            skLineSegment(sketch, "E6.58.1", {"start": v(7.16, 27.45) * mm, "end": v(5.56, 25.3) * mm});
            skLineSegment(sketch, "E6.58.2", {"start": v(4.62, 28) * mm, "end": v(5.2, 25.37) * mm});
            skArc(sketch, "E6.58.3", {"start": v(5.2, 25.37) * mm, "mid": v(5.36, 25.22) * mm, "end": v(5.56, 25.3) * mm});
            skArc(sketch, "E6.58.4", {"start": v(4.62, 28) * mm, "mid": v(4.46, 28.15) * mm, "end": v(4.25, 28.05) * mm});
            skPoint(sketch, "E6.59.0", {"position": v(2.67, 25.36) * mm});
            skLineSegment(sketch, "E6.59.1", {"start": v(4.25, 28.05) * mm, "end": v(2.89, 25.74) * mm});
            skLineSegment(sketch, "E6.59.2", {"start": v(1.67, 28.32) * mm, "end": v(2.53, 25.78) * mm});
            skArc(sketch, "E6.59.3", {"start": v(2.53, 25.78) * mm, "mid": v(2.7, 25.64) * mm, "end": v(2.89, 25.74) * mm});
            skArc(sketch, "E6.59.4", {"start": v(1.67, 28.32) * mm, "mid": v(1.5, 28.46) * mm, "end": v(1.3, 28.34) * mm});
            skSolve(sketch);
        }
        {
            var Q0;
            Q0 = qSketchRegion(id + "F2", true);
            extrude(context, id + "F3", {"entities" : qUnion([Q0]), "operationType" : NewBodyOperationType.REMOVE, "oppositeDirection" : true, "depth" : 35 * mm});
        }
        {
            var Q0;
            Q0=qCreatedBy(makeId("Right.planeOp"),FACE);
            var sketch = newSketch(context, id + "F4", { "sketchPlane" : qUnion([Q0])});
            skCircle(sketch, "E7", {"center": v(0, 0) * mm, "radius": 3.05 * mm});
            skSolve(sketch);
        }
        {
            var Q0;
            Q0 = qSketchRegion(id + "F4", true);
            extrude(context, id + "F5", {"entities" : qUnion([Q0]), "operationType" : NewBodyOperationType.REMOVE, "endBound" : BoundingType.THROUGH_ALL, "depth" : 25 * mm});
        }
    });
